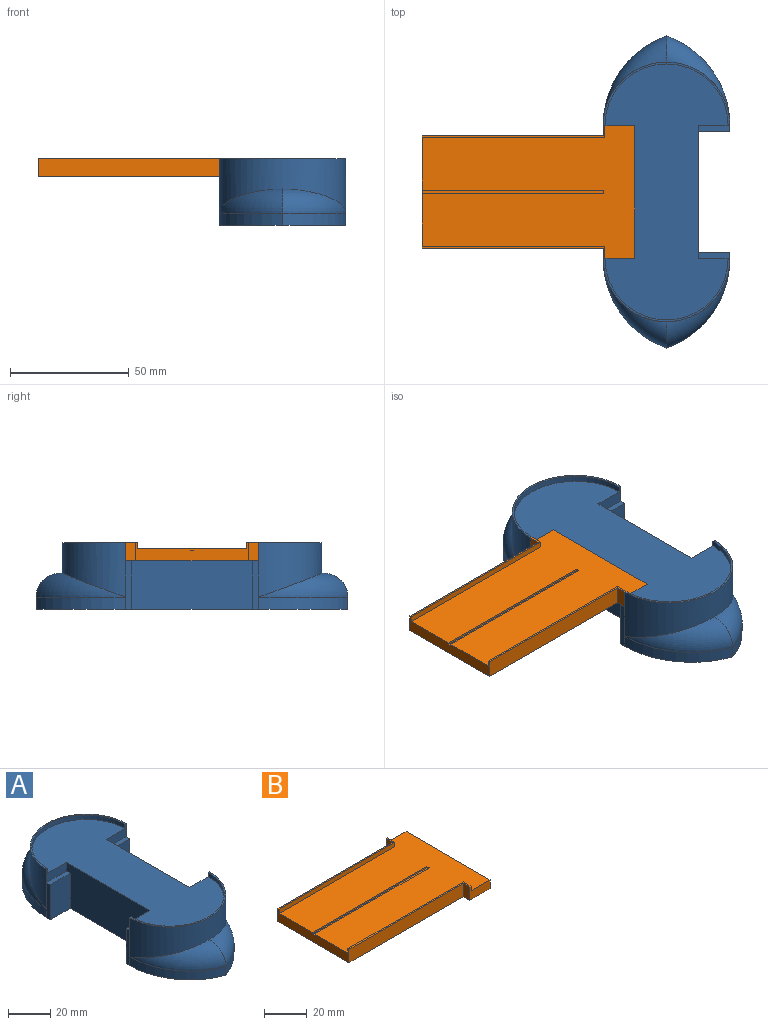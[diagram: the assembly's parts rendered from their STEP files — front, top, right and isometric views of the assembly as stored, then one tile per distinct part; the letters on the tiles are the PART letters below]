
ASSEMBLY  parts=2 mates=1
PART A: 36 faces, bbox 59.9x137.5x27.9 mm
  f0: plane 107.7x51.82mm, normal (0,0,1), area 3599mm2, adj f1,f2,f3,f5,f6,f7,f32,f34
  f1: plane 55.88x25.4mm, normal (-1,0,0), area 1316.1mm2, adj f0,f2,f3,f9,f20,f22,f27,f28
  f2: plane 13.34x7.62mm, normal (0,-1,0), area 69.7mm2, adj f0,f1,f8,f28,f34,f35
  f3: plane 13.34x7.62mm, normal (0,1,0), area 69.7mm2, adj f0,f1,f4,f22,f32,f33
  f4: cylinder r=26.67mm len=53.34mm, axis (0,0,-1), area 1387.9mm2, adj f3,f5,f15,f18,f19,f21,f24,f33
  f5: plane 13.34x7.62mm, normal (0,1,0), area 69.7mm2, adj f0,f4,f6,f25,f32,f33
  f6: plane 55.88x25.4mm, normal (1,0,0), area 1316.1mm2, adj f0,f5,f7,f9,f23,f25,f29,f31
  f7: plane 13.34x7.62mm, normal (0,-1,0), area 69.7mm2, adj f0,f6,f8,f31,f34,f35
  f8: cylinder r=26.67mm len=53.34mm, axis (0,0,-1), area 1387.9mm2, adj f2,f7,f12,f16,f17,f26,f30,f35
  f9: plane 131.31x53.34mm, normal (0,0,-1), area 4559.9mm2, adj f1,f6,f10,f11,f13,f14,f20,f21
  f10: cylinder r=40mm len=37.72mm, axis (0,0,-1), area 250.2mm2, adj f9,f11,f17,f30
  f11: cylinder r=40mm len=37.72mm, axis (0,0,-1), area 250.2mm2, adj f9,f10,f16,f26
  f12: plane 0.12x0.03mm, normal (0,0,1), area 0mm2, adj f8,f16,f17
  f13: cylinder r=40mm len=37.72mm, axis (0,0,-1), area 250.2mm2, adj f9,f14,f19,f21
  f14: cylinder r=40mm len=37.72mm, axis (0,0,-1), area 250.2mm2, adj f9,f13,f18,f24
  f15: plane 0.12x0.03mm, normal (0,0,1), area 0mm2, adj f4,f18,f19
  f16: torus R=29.84mm, axis (0,0,1), area 385.4mm2, adj f8,f11,f12,f17
  f17: torus R=29.84mm, axis (0,0,1), area 385.4mm2, adj f8,f10,f12,f16
  f18: torus R=29.84mm, axis (0,0,1), area 385.4mm2, adj f4,f14,f15,f19
  f19: torus R=29.84mm, axis (0,0,1), area 385.4mm2, adj f4,f13,f15,f18
  f20: plane 20.32x13.34mm, normal (0,1,0), area 271mm2, adj f1,f9,f21,f22
  f21: plane 20.32x2.54mm, normal (-1,0,0), area 51.6mm2, adj f4,f9,f13,f20,f22
  f22: plane 13.34x2.54mm, normal (0,0,1), area 33.9mm2, adj f1,f3,f20,f21
  f23: plane 20.32x13.34mm, normal (0,1,0), area 271mm2, adj f6,f9,f24,f25
  f24: plane 20.32x2.54mm, normal (1,0,0), area 51.6mm2, adj f4,f9,f14,f23,f25
  f25: plane 13.34x2.54mm, normal (0,0,1), area 33.9mm2, adj f5,f6,f23,f24
  f26: plane 20.32x2.54mm, normal (-1,0,0), area 51.6mm2, adj f8,f9,f11,f27,f28
  f27: plane 20.32x13.34mm, normal (0,-1,0), area 271mm2, adj f1,f9,f26,f28
  f28: plane 13.34x2.54mm, normal (0,0,1), area 33.9mm2, adj f1,f2,f26,f27
  f29: plane 20.32x13.34mm, normal (0,-1,0), area 271mm2, adj f6,f9,f30,f31
  f30: plane 20.32x2.54mm, normal (1,0,0), area 51.6mm2, adj f8,f9,f10,f29,f31
  f31: plane 13.34x2.54mm, normal (0,0,1), area 33.9mm2, adj f6,f7,f29,f30
  f32: cylinder r=25.91mm len=51.82mm, axis (0,0,-1), area 206.7mm2, adj f0,f3,f5,f33
  f33: plane 53.34x26.67mm, normal (0,0,1), area 62.9mm2, adj f3,f4,f5,f32
  f34: cylinder r=25.91mm len=51.82mm, axis (0,0,-1), area 206.7mm2, adj f0,f2,f7,f35
  f35: plane 53.34x26.67mm, normal (0,0,1), area 62.9mm2, adj f2,f7,f8,f34
PART B: 20 faces, bbox 89.5x55.9x7.6 mm
  f0: plane 89.54x55.88mm, normal (0,0,1), area 4105.2mm2, adj f3,f4,f5,f8,f9,f10,f11,f13
  f1: plane 76.2x7.62mm, normal (0,-1,0), area 580.6mm2, adj f2,f8,f12,f15
  f2: plane 7.62x4.32mm, normal (-1,0,0), area 32.9mm2, adj f1,f3,f12,f15
  f3: plane 13.34x7.62mm, normal (0,-1,0), area 69.7mm2, adj f0,f2,f4,f12,f13,f15
  f4: plane 55.88x5.08mm, normal (1,0,0), area 283.9mm2, adj f0,f3,f5,f12
  f5: plane 13.34x7.62mm, normal (0,1,0), area 69.7mm2, adj f0,f4,f6,f12,f17,f18
  f6: plane 7.62x4.32mm, normal (-1,0,0), area 32.9mm2, adj f5,f7,f12,f18
  f7: plane 76.2x7.62mm, normal (0,1,0), area 580.6mm2, adj f6,f8,f12,f18
  f8: plane 47.24x7.62mm, normal (-1,0,0), area 242.7mm2, adj f0,f1,f7,f9,f11,f12,f14,f15
  f9: plane 76.2x0.76mm, normal (0,-1,0), area 58.1mm2, adj f0,f8,f10,f19
  f10: plane 1.52x0.76mm, normal (-1,0,0), area 1.2mm2, adj f0,f9,f11,f19
  f11: plane 76.2x0.76mm, normal (0,1,0), area 58.1mm2, adj f0,f8,f10,f19
  f12: plane 89.54x55.88mm, normal (0,0,-1), area 4345.2mm2, adj f1,f2,f3,f4,f5,f6,f7,f8
  f13: plane 5.08x2.54mm, normal (1,0,0), area 12.9mm2, adj f0,f3,f14,f15
  f14: plane 76.96x2.54mm, normal (0,1,0), area 195.5mm2, adj f0,f8,f13,f15
  f15: plane 76.96x5.08mm, normal (0,0,1), area 61.9mm2, adj f1,f2,f3,f8,f13,f14
  f16: plane 76.96x2.54mm, normal (0,-1,0), area 195.5mm2, adj f0,f8,f17,f18
  f17: plane 5.08x2.54mm, normal (1,0,0), area 12.9mm2, adj f0,f5,f16,f18
  f18: plane 76.96x5.08mm, normal (0,0,1), area 61.9mm2, adj f5,f6,f7,f8,f16,f17
  f19: plane 76.2x1.52mm, normal (0,0,1), area 116.1mm2, adj f8,f9,f10,f11
PLACE A t=(4.99,1.19,-16.51)mm
PLACE B t=(-59.78,1.19,3.81)mm
MATE fastened B.f4 <-> A.f1  axis (1,0,0) through (-8.35,1.19,8.89)mm
